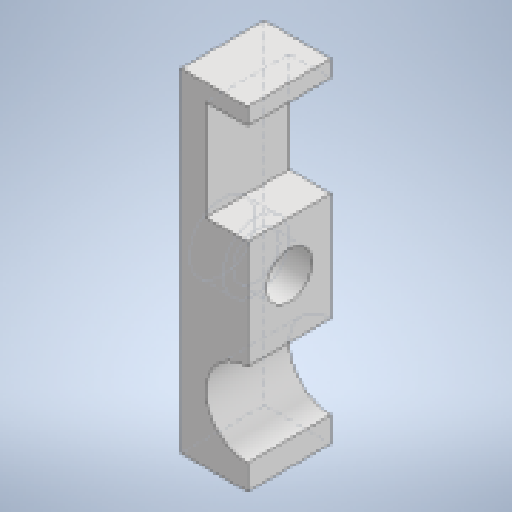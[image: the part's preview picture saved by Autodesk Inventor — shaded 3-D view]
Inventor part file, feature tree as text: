
AUTODESK INVENTOR PART (.ipt)
format: ipt  version: 2023 (Build 270158000, 158)  size: 168,448 bytes
history: native  units: mm
features: extrude x3, sketch x3
ambient origin geometry x8: Origin, YZ Plane, XZ Plane, XY Plane, X Axis, Y Axis, Z Axis, Center Point
bodies: Solid1 (feature_tree)
feature tree (6):
  extrude  "Extrusion1"  Depth=4.0mm
  extrude  "Extrusion2"  Depth=5.0mm
  extrude  "Extrusion3"  Depth=4.0mm
  sketch  "Sketch1"  dims[d0=20.0mm d1=4.0mm]
  sketch  "Sketch3"  dims[d2=5.0mm d3=5.0mm]
  sketch  "Sketch4"  dims[d4=4.0mm d5=4.0mm d6=3.0mm d7=3.0mm d8=5.0mm d9=0.0mm d10=10.0mm d11=2.5mm d12=20.0mm d13=2.75mm d14=20.0mm d15=0.0mm d16=4.0mm d17=2.0mm d18=0.0mm]
